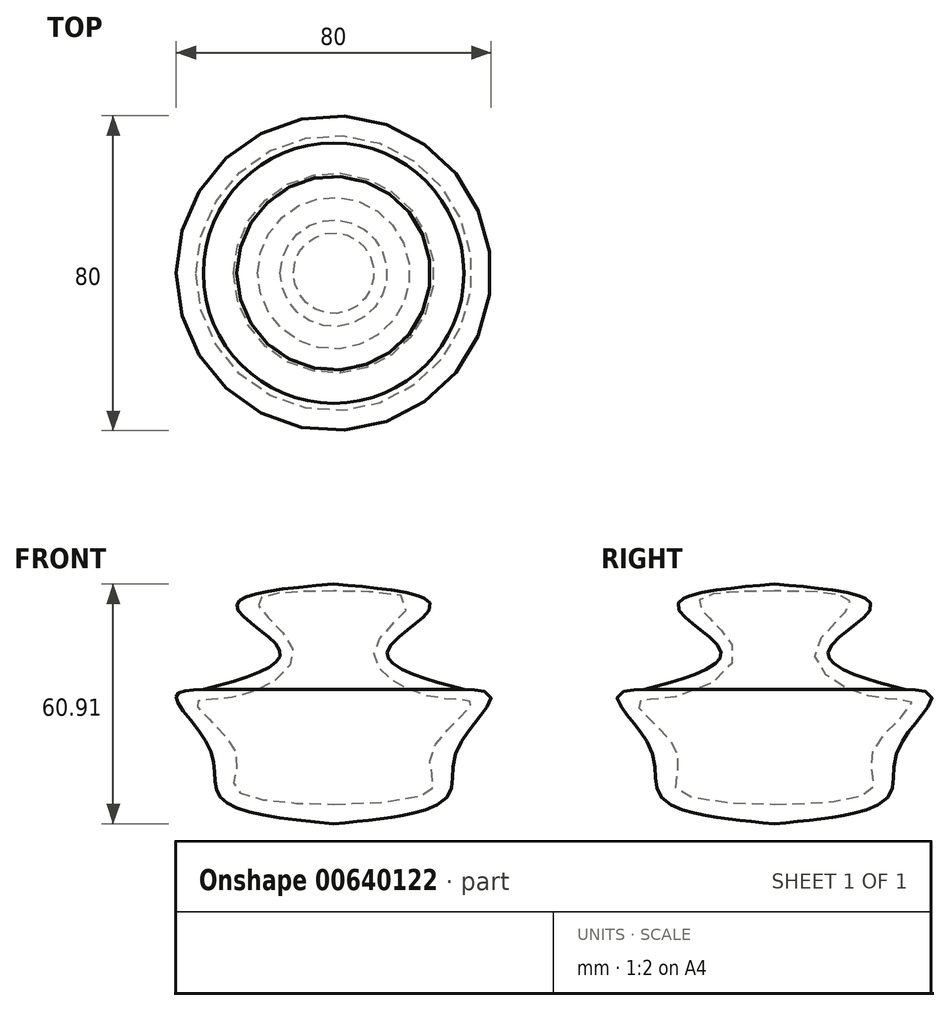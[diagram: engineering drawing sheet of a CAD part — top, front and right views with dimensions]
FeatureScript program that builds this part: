
annotation { "Feature Type Name" : "Feature", "Feature Type Description" : "" }
export const myFeature = defineFeature(function(context is Context, id is Id, definition is map)
    precondition{}
    {
        {
            var Q0;
            Q0=qCreatedBy(makeId("Front.planeOp"),FACE);
            var sketch = newSketch(context, id + "F0", { "sketchPlane" : qUnion([Q0])});
            skLineSegment(sketch, "E0", {"start": v(0, 35.04) * mm, "end": v(0, 33.27) * mm});
            skFitSpline(sketch, "E1", {"points": [v(0, 35.04) * mm, v(-24.58, 29.1) * mm, v(-13.66, 18.01) * mm, v(-33.09, 8.22) * mm], "startDerivative": vector(-103.85, -8.94) * mm, "endDerivative": vector(-90.32, -24.49) * mm});
            skFitSpline(sketch, "E2", {"points": [v(-33.09, 8.22) * mm, v(-40, 6.45) * mm, v(-31.32, -7.2) * mm, v(-28.91, -18.92) * mm, v(0, -25.87) * mm], "startDerivative": vector(-58.74, -1.42) * mm, "endDerivative": vector(109.48, -10.33) * mm});
            skFitSpline(sketch, "E3", {"points": [v(0, 33.27) * mm, v(-19.28, 30.05) * mm, v(-10.29, 17.85) * mm, v(-25.38, 6.29) * mm, v(-35.01, 4.58) * mm, v(-24.58, -8.48) * mm, v(-24.58, -17.48) * mm, v(14.92, -20.2) * mm], "startDerivative": vector(-209.75, -2.24) * mm, "endDerivative": vector(78.26, 13.16) * mm});
            skLineSegment(sketch, "E4.trimOffspring", {"start": v(0, -20.9) * mm, "end": v(0, -25.87) * mm});
            skSolve(sketch);
        }
        {
            var Q0;
            Q0=makeQuery(id+"F0.imprint","IMPRINT",FACE,{"disambiguationData":[TD([[makeQuery(id+"F0.imprint","IMPRINT",EDGE,{"derivedFrom":sQuery(id+"F0.wireOp",EDGE,"E0")}),-1.0]])]});
            var Q1;
            Q1=sQuery(id+"F0.wireOp",EDGE,"E4.trimOffspring");
            revolve(context, id + "F1", {"entities" : qUnion([Q0]), "axis" : qUnion([Q1]), "revolveType" : RevolveType.FULL});
        }
    });
